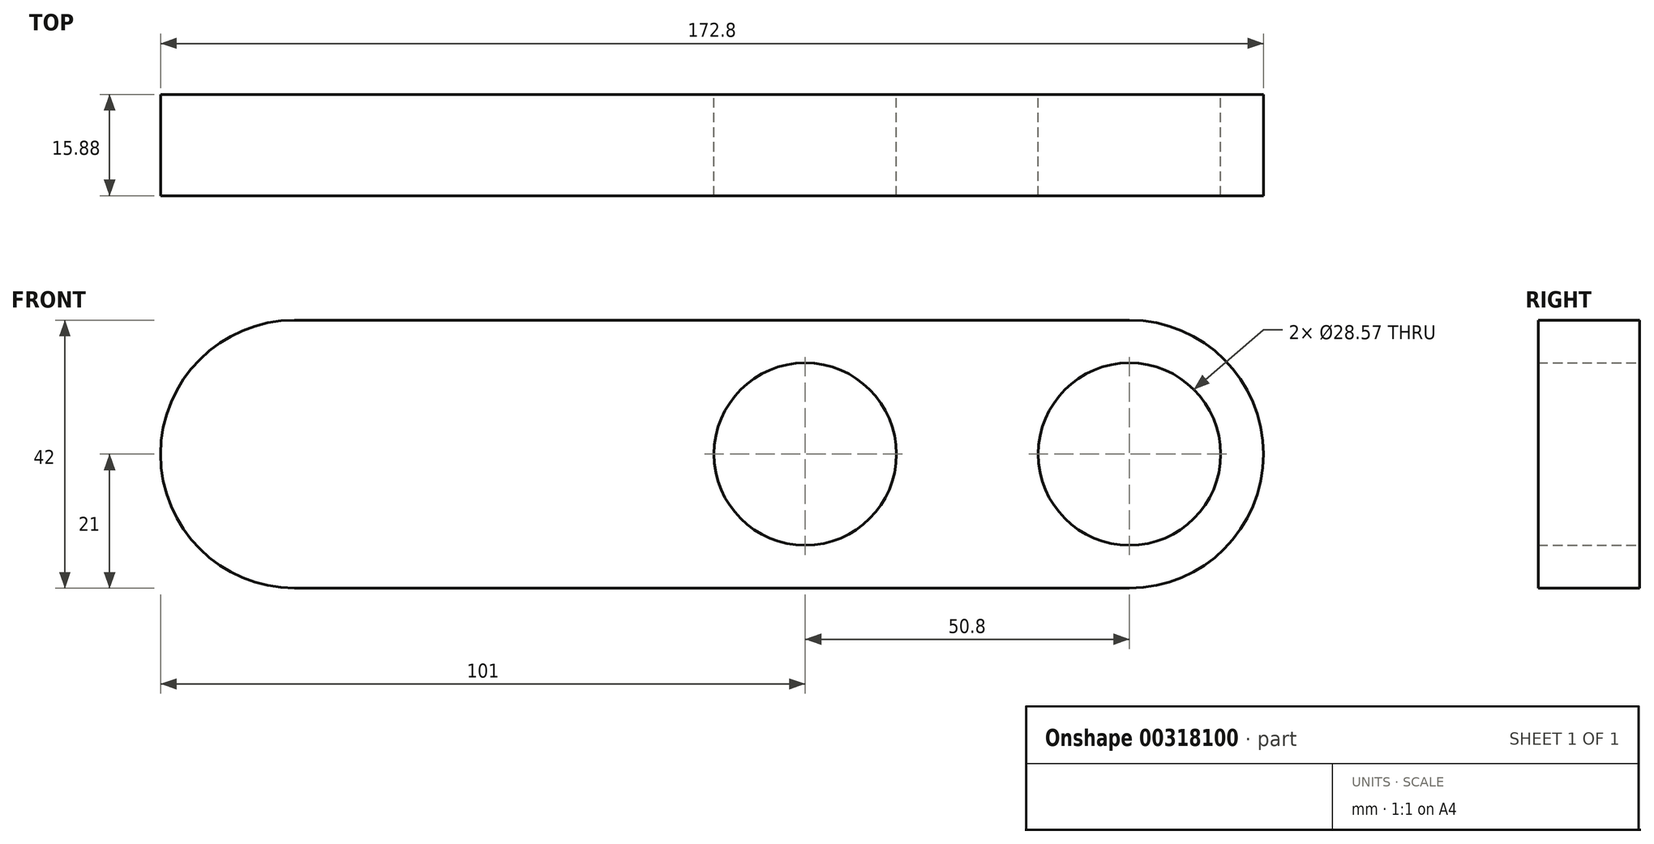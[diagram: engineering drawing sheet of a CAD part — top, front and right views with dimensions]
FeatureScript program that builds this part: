
annotation { "Feature Type Name" : "Feature", "Feature Type Description" : "" }
export const myFeature = defineFeature(function(context is Context, id is Id, definition is map)
    precondition{}
    {
        {
            var Q0;
            Q0=qCreatedBy(makeId("Front.planeOp"),FACE);
            var sketch = newSketch(context, id + "F0", { "sketchPlane" : qUnion([Q0])});
            skLineSegment(sketch, "E0", {"start": v(0, 0) * mm, "end": v(25.4, 0) * mm, "construction": true});
            skLineSegment(sketch, "E1", {"start": v(0, 0) * mm, "end": v(-25.4, 0) * mm, "construction": true});
            skCircle(sketch, "E2", {"center": v(-25.4, 0) * mm, "radius": 14.29 * mm});
            skCircle(sketch, "E3", {"center": v(25.4, 0) * mm, "radius": 14.29 * mm});
            skArc(sketch, "E4", {"start": v(25.4, -21) * mm, "mid": v(46.4, 0) * mm, "end": v(25.4, 21) * mm});
            skLineSegment(sketch, "E5", {"start": v(25.4, 21) * mm, "end": v(-105.4, 21) * mm});
            skLineSegment(sketch, "E6", {"start": v(25.4, -21) * mm, "end": v(-105.4, -21) * mm});
            skArc(sketch, "E7", {"start": v(-105.4, 21) * mm, "mid": v(-126.4, 0) * mm, "end": v(-105.4, -21) * mm});
            skSolve(sketch);
        }
        {
            var Q0;
            Q0 = qSketchRegion(id + "F0", true);
            extrude(context, id + "F1", {"entities" : qUnion([Q0]), "depth" : 15.88 * mm, "offsetDistance" : 25.4 * mm});
        }
    });
